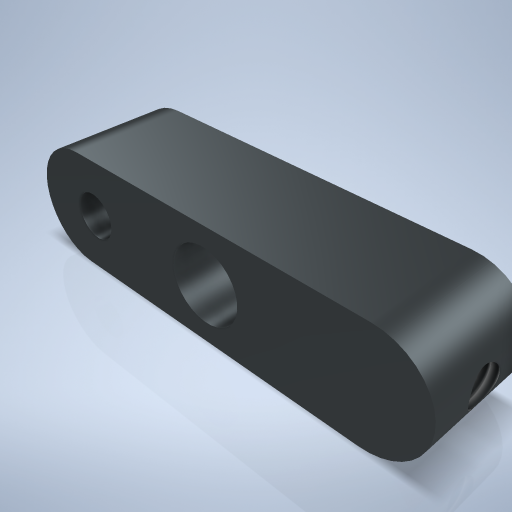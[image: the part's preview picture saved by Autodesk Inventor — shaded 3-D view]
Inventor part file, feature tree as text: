
AUTODESK INVENTOR PART (.ipt)
format: ipt  version: 2024.2 (Build 282272000, 272)  size: 267,264 bytes
history: native  units: mm
features: sketch x4, hole x3, extrude x1, plane x1
ambient origin geometry x8: Origin, YZ Plane, XZ Plane, XY Plane, X Axis, Y Axis, Z Axis, Center Point
bodies: Volumenkörper1 (feature_tree)
feature tree (9):
  extrude  "Extrusion1"  Depth=5.0mm
  hole  "Bohrung1"  [1 undecoded]
  hole  "Bohrung2"  [1 undecoded]
  plane  "Arbeitsebene1"
  hole  "Bohrung3"  [1 undecoded]
  sketch  "Skizze1"  dims[d1=38.0mm d2=5.0mm]
  sketch  "Skizze2"  dims[d3=10.0mm d4=0.0mm]
  sketch  "Skizze3"  dims[d5=6.5mm d6=6.0mm d7=4.0mm d8=2.0mm d9=90.0deg d10=8.0mm d11=0.0mm]
  sketch  "Skizze4"  dims[d12=4.0mm d13=6.0mm d14=4.0mm d15=2.0mm d16=90.0deg d17=8.0mm d18=0.0mm d19=12.5mm d20=19.0mm d21=5.0mm d22=3.242mm d23=8.0mm d24=4.0mm d25=2.0mm d26=90.0deg d27=15.75mm d28=20.594885mm]
note: 3 required parameter values undecoded (feature->parameter linkage not recoverable at this tier; creation-order binding heuristic only, values carry confidence <= 0.55)
